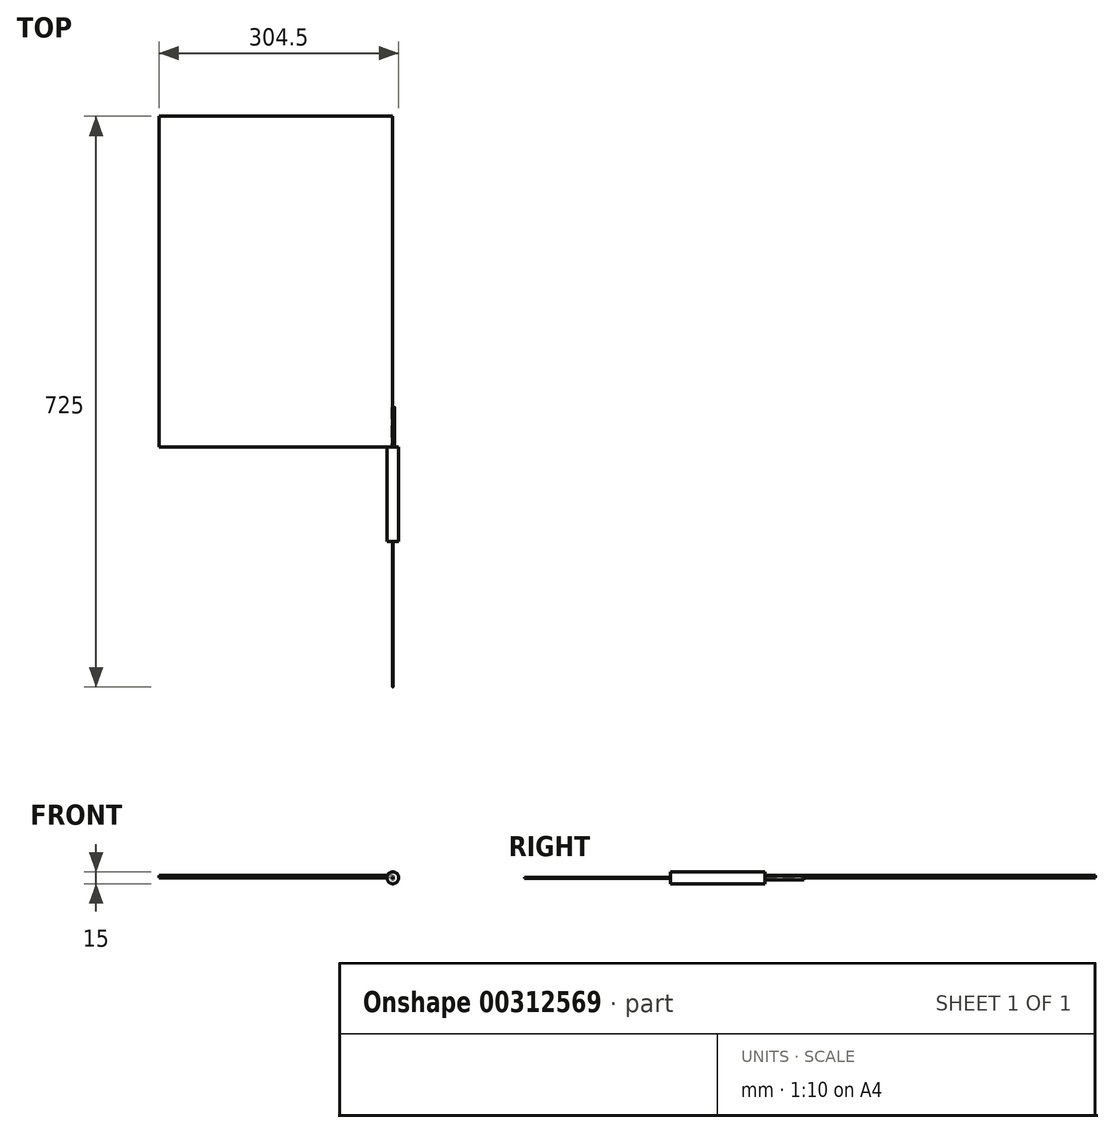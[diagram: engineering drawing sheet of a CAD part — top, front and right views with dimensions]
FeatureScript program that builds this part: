
annotation { "Feature Type Name" : "Feature", "Feature Type Description" : "" }
export const myFeature = defineFeature(function(context is Context, id is Id, definition is map)
    precondition{}
    {
        {
            var Q0;
            Q0=qCreatedBy(makeId("Front.planeOp"),FACE);
            var sketch = newSketch(context, id + "F0", { "sketchPlane" : qUnion([Q0])});
            skCircle(sketch, "E0", {"center": v(0, 0) * mm, "radius": 7.5 * mm});
            skSolve(sketch);
        }
        {
            var Q0;
            Q0=makeQuery(id+"F0.imprint","IMPRINT",FACE,{"disambiguationData":[TD([[makeQuery(id+"F0.imprint","IMPRINT",EDGE,{"derivedFrom":sQuery(id+"F0.wireOp",EDGE,"E0")}),1.0]])]});
            extrude(context, id + "F1", {"entities" : qUnion([Q0]), "depth" : 120 * mm});
        }
        {
            var Q0;
            Q0=makeQuery(id+"F1.opExtrude","CAP_FACE",FACE,{"disambiguationData":[OSD([sQuery(id+"F0.wireOp",EDGE,"E0")])],"isStart":false});
            var sketch = newSketch(context, id + "F2", { "sketchPlane" : qUnion([Q0])});
            skSolve(sketch);
        }
        {
            var Q0;
            Q0=makeQuery(id+"F2.imprint","IMPRINT",FACE,{"disambiguationData":[TD([[makeQuery(id+"F2.imprint","IMPRINT",EDGE,{"derivedFrom":makeQuery(id+"F1.opExtrude","CAP_EDGE",EDGE,{"disambiguationData":[OSD([sQuery(id+"F0.wireOp",EDGE,"E0")])],"isStart":false})}),1.0]])]});
            var sketch = newSketch(context, id + "F3", { "sketchPlane" : qUnion([Q0])});
            skCircle(sketch, "E1", {"center": v(0, 0) * mm, "radius": 0.5 * mm});
            skSolve(sketch);
        }
        {
            var Q0;
            Q0 = qSketchRegion(id + "F3", true);
            extrude(context, id + "F4", {"entities" : qUnion([Q0]), "depth" : 185 * mm});
        }
        {
            var Q0;
            Q0=qCreatedBy(makeId("Front.planeOp"),FACE);
            var sketch = newSketch(context, id + "F5", { "sketchPlane" : qUnion([Q0])});
            skCircle(sketch, "E2", {"center": v(0, 0) * mm, "radius": 2.5 * mm});
            skSolve(sketch);
        }
        {
            var Q0;
            Q0 = qSketchRegion(id + "F5", true);
            extrude(context, id + "F6", {"entities" : qUnion([Q0]), "oppositeDirection" : true, "depth" : 50 * mm, "offsetDistance" : 25 * mm});
        }
        {
            var Q0;
            Q0=qCreatedBy(makeId("Top.planeOp"),FACE);
            var sketch = newSketch(context, id + "F7", { "sketchPlane" : qUnion([Q0])});
            skLineSegment(sketch, "E3.bottom", {"start": v(0, 0) * mm, "end": v(-297, 0) * mm});
            skLineSegment(sketch, "E3.top", {"start": v(0, 420) * mm, "end": v(-297, 420) * mm});
            skLineSegment(sketch, "E3.left", {"start": v(0, 0) * mm, "end": v(0, 420) * mm});
            skLineSegment(sketch, "E3.right", {"start": v(-297, 0) * mm, "end": v(-297, 420) * mm});
            skSolve(sketch);
        }
        {
            var Q0;
            Q0=makeQuery(id+"F7.imprint","IMPRINT",FACE,{"disambiguationData":[TD([[makeQuery(id+"F7.imprint","IMPRINT",EDGE,{"derivedFrom":sQuery(id+"F7.wireOp",EDGE,"E3.bottom")}),-1.0]])]});
            extrude(context, id + "F8", {"entities" : qUnion([Q0]), "depth" : 3 * mm, "offsetDistance" : 25 * mm});
        }
    });
